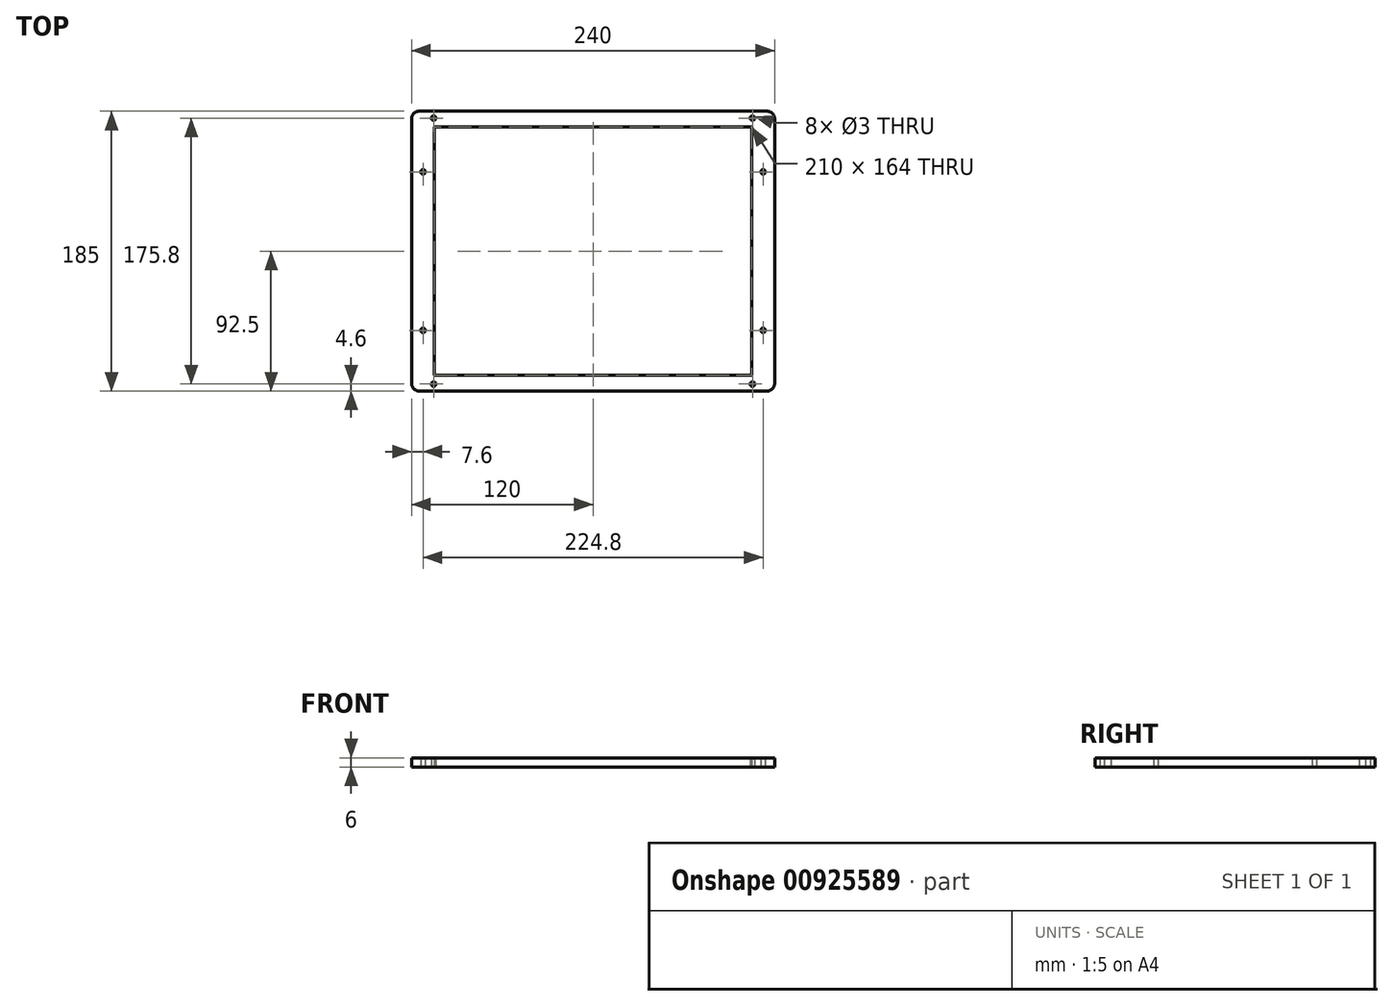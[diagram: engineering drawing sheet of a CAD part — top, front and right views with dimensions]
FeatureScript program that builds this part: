
annotation { "Feature Type Name" : "Feature", "Feature Type Description" : "" }
export const myFeature = defineFeature(function(context is Context, id is Id, definition is map)
    precondition{}
    {
        {
            var Q0;
            Q0=qCreatedBy(makeId("Top.planeOp"),FACE);
            var sketch = newSketch(context, id + "F0", { "sketchPlane" : qUnion([Q0])});
            skLineSegment(sketch, "E0.bottom", {"start": v(115, -92.5) * mm, "end": v(-115, -92.5) * mm});
            skLineSegment(sketch, "E0.top", {"start": v(115, 92.5) * mm, "end": v(-115, 92.5) * mm});
            skLineSegment(sketch, "E0.left", {"start": v(120, -87.5) * mm, "end": v(120, 87.5) * mm});
            skLineSegment(sketch, "E0.right", {"start": v(-120, -87.5) * mm, "end": v(-120, 87.5) * mm});
            skPoint(sketch, "E0.middle", {"position": v(0, 0) * mm});
            skLineSegment(sketch, "E1.bottom", {"start": v(105, -82) * mm, "end": v(-105, -82) * mm});
            skLineSegment(sketch, "E1.top", {"start": v(105, 82) * mm, "end": v(-105, 82) * mm});
            skLineSegment(sketch, "E1.left", {"start": v(105, -82) * mm, "end": v(105, 82) * mm});
            skLineSegment(sketch, "E1.right", {"start": v(-105, -82) * mm, "end": v(-105, 82) * mm});
            skCircle(sketch, "E2", {"center": v(-105.4, 87.9) * mm, "radius": 1.5 * mm});
            skCircle(sketch, "E3", {"center": v(105.4, 87.9) * mm, "radius": 1.5 * mm});
            skCircle(sketch, "E4", {"center": v(105.4, -87.9) * mm, "radius": 1.5 * mm});
            skCircle(sketch, "E5", {"center": v(-105.4, -87.9) * mm, "radius": 1.5 * mm});
            skLineSegment(sketch, "E6", {"start": v(0, -35.76) * mm, "end": v(0, 32.72) * mm, "construction": true});
            skLineSegment(sketch, "E7", {"start": v(-32.9, 0) * mm, "end": v(32.9, 0) * mm, "construction": true});
            skPoint(sketch, "E8.visualSharp", {"position": v(-120, 92.5) * mm});
            skArc(sketch, "E8.filletArc", {"start": v(-115, 92.5) * mm, "mid": v(-118.54, 91.04) * mm, "end": v(-120, 87.5) * mm});
            skPoint(sketch, "E9.visualSharp", {"position": v(120, 92.5) * mm});
            skArc(sketch, "E9.filletArc", {"start": v(120, 87.5) * mm, "mid": v(118.54, 91.04) * mm, "end": v(115, 92.5) * mm});
            skPoint(sketch, "E10.visualSharp", {"position": v(120, -92.5) * mm});
            skArc(sketch, "E10.filletArc", {"start": v(115, -92.5) * mm, "mid": v(118.54, -91.04) * mm, "end": v(120, -87.5) * mm});
            skPoint(sketch, "E11.visualSharp", {"position": v(-120, -92.5) * mm});
            skArc(sketch, "E11.filletArc", {"start": v(-120, -87.5) * mm, "mid": v(-118.54, -91.04) * mm, "end": v(-115, -92.5) * mm});
            skCircle(sketch, "E12", {"center": v(-112.4, 52.4) * mm, "radius": 1.5 * mm});
            skCircle(sketch, "E13", {"center": v(-112.4, -52.4) * mm, "radius": 1.5 * mm});
            skCircle(sketch, "E14", {"center": v(112.4, 52.4) * mm, "radius": 1.5 * mm});
            skCircle(sketch, "E15", {"center": v(112.4, -52.4) * mm, "radius": 1.5 * mm});
            skSolve(sketch);
        }
        {
            var Q0;
            Q0 = qSketchRegion(id + "F0", true);
            extrude(context, id + "F1", {"entities" : qUnion([Q0]), "depth" : 6 * mm, "offsetDistance" : 25 * mm});
        }
    });
